# Revit family: BTKP-090X30-300-840-xxx-SWF
name_source: partatom
category: Leuchten
revit_build: Autodesk Revit 2017 (Build: 20190508_0315(x64)
units: mm (PartAtom-declared; Revit-internal decimal feet)

## family parameters
Basisbauteil = Fläche
Beim Laden mit Abzugskörper schneiden = Nein
Bemaßung runder Anschluss = Durchmesser verwenden
Gemeinsam genutzt = Nein
Lichtquelle = Ja
OmniClass-Nummer = 23.80.70.11
OmniClass-Titel = Luminaries for Internal Lighting
Raumberechnungspunkt = Nein
Teiletyp = Normal

## types (4) — shared parameters
Baugruppenkennzeichen = D5020200
Emissionsform beim Rendern sichtbar = Nein
Farbfilter = 16777215
Farbtemperaturverschiebung bei Dämpfen der Lampe = <Keine Auswahl>
Hersteller = RIDI Leuchten GmbH
Lampe = LED
Neigungswinkel = 90.00°
Scheinlast = 19 VA
URL = www.spectral.de
Von Breite des Rechtecks ausssenden = 892 mm  [stored 2.92651 ft]
Von Länge des Rechtecks aussenden = 31 mm  [stored 0.101706 ft]
brand = Spectral
conformity mark = CE
electrical safety class = 1
height = 300 mm
ingress protection (IP) code = IP20
length = 598 mm  [stored 1.96194 ft]
nominal frequency = 50-60Hz
nominal voltage = 230
rated input power = 19
voltage type (AC, DC, UC) = AC
weight = 5.6 kg
width = 42 mm  [stored 0.137795 ft]
zero-valued in all types: Vorgabe-Ansicht

## per-type parameters (varying)
| type | Datei für fotometrisches Netz | Modell |
| BTKP 090X30/300-840 DPO-SWF | BTKP 150x30500-840 DPO-SWF.IES | SPK0620004BL |
| BTKP 090X30/300-840 DPO-DA-SWF | BTKP 150x30500-840 DPO-SWF.IES | SPK0630004BL |
| BTKP 090X30/300-840 MPS-SWF | BTKP 150x30500-840 MPS-SWF.IES | SPK0620005BL |
| BTKP 090X30/300-840 MPS-DA-SWF | BTKP 150x30500-840 MPS-SWF.IES | SPK0630005BL |

note: column(s) folded — value = type name in every type: product name

note: [stored X ft] marks values corroborated as IEEE doubles in the binary element streams (Revit-internal decimal feet)
